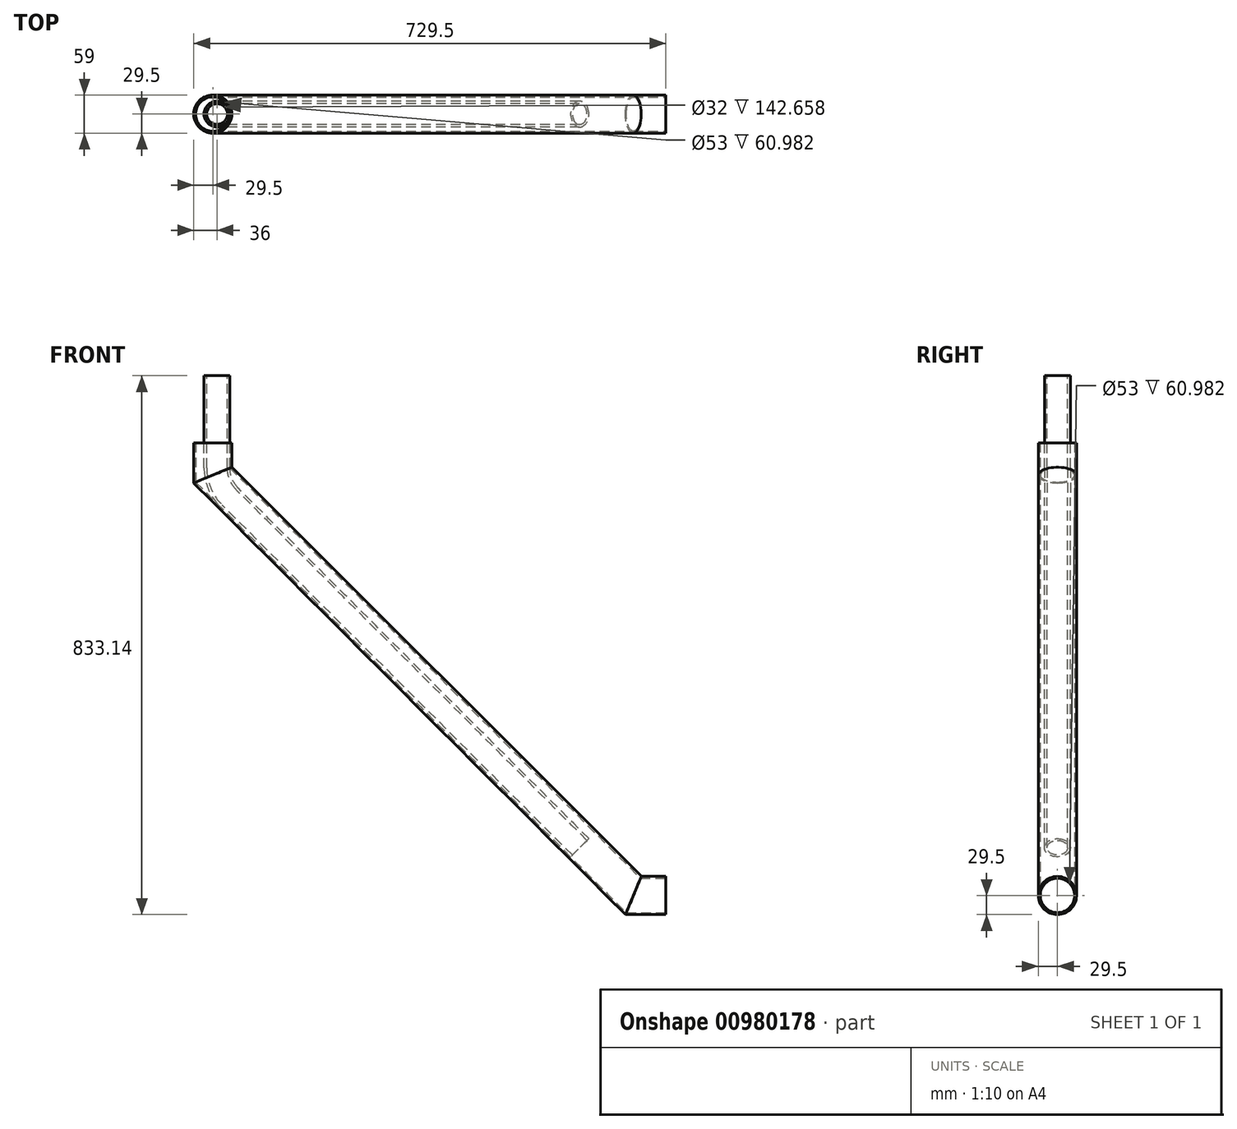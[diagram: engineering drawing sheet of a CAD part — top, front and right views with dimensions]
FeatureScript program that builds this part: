
annotation { "Feature Type Name" : "Feature", "Feature Type Description" : "" }
export const myFeature = defineFeature(function(context is Context, id is Id, definition is map)
    precondition{}
    {
        {
            var Q0;
            Q0=qCreatedBy(makeId("Top.planeOp"),FACE);
            var sketch = newSketch(context, id + "F0", { "sketchPlane" : qUnion([Q0])});
            skCircle(sketch, "E0", {"center": v(0, 0) * mm, "radius": 26.5 * mm});
            skCircle(sketch, "E1", {"center": v(0, 0) * mm, "radius": 29.5 * mm});
            skCircle(sketch, "E2", {"center": v(0, 0) * mm, "radius": 20 * mm, "construction": true});
            skSolve(sketch);
        }
        {
            var Q0;
            Q0=qCreatedBy(makeId("Front.planeOp"),FACE);
            var sketch = newSketch(context, id + "F1", { "sketchPlane" : qUnion([Q0])});
            skLineSegment(sketch, "E3", {"start": v(0, 0) * mm, "end": v(0, -50) * mm});
            skLineSegment(sketch, "E4", {"start": v(0, -50) * mm, "end": v(650, -700) * mm});
            skLineSegment(sketch, "E5", {"start": v(650, -700) * mm, "end": v(700, -700) * mm});
            skSolve(sketch);
        }
        {
            var Q0;
            Q0 = qSketchRegion(id + "F0", true);
            var Q1;
            Q1 = qConstructionFilter(qBodyType(qCreatedBy(id + "F1" ,EDGE), BodyType.WIRE), ConstructionObject.NO);
            sweep(context, id + "F2", {"profiles" : qUnion([Q0]), "path" : qUnion([Q1])});
        }
        {
            var Q0;
            Q0=qCreatedBy(makeId("Front.planeOp"),FACE);
            var sketch = newSketch(context, id + "F3", { "sketchPlane" : qUnion([Q0])});
            skLineSegment(sketch, "E6", {"start": v(50.18, -137.65) * mm, "end": v(-26.5, -60.98) * mm, "construction": true});
            skLineSegment(sketch, "E7", {"start": v(-26.5, -60.98) * mm, "end": v(-26.5, 0) * mm, "construction": true});
            skLineSegment(sketch, "E8", {"start": v(-26.5, 0) * mm, "end": v(0, 0) * mm, "construction": true});
            skLineSegment(sketch, "E9", {"start": v(0, 0) * mm, "end": v(26.5, 0) * mm, "construction": true});
            skLineSegment(sketch, "E10", {"start": v(26.5, 0) * mm, "end": v(26.5, -39.02) * mm, "construction": true});
            skLineSegment(sketch, "E11", {"start": v(26.5, -39.02) * mm, "end": v(93.16, -105.68) * mm, "construction": true});
            skLineSegment(sketch, "E12", {"start": v(0, 0) * mm, "end": v(0, -50) * mm, "construction": true});
            skLineSegment(sketch, "E13", {"start": v(0, -50) * mm, "end": v(72.4, -122.4) * mm, "construction": true});
            skLineSegment(sketch, "E14", {"start": v(6.5, 0) * mm, "end": v(6.5, -39.02) * mm});
            skArc(sketch, "E15", {"start": v(6.5, -39.02) * mm, "mid": v(11.4, -63.66) * mm, "end": v(25.36, -84.55) * mm});
            skLineSegment(sketch, "E16", {"start": v(25.36, -84.55) * mm, "end": v(566.96, -626.16) * mm});
            skLineSegment(sketch, "E17", {"start": v(6.5, -39.02) * mm, "end": v(26.5, -39.02) * mm, "construction": true});
            skLineSegment(sketch, "E18", {"start": v(6.5, 0) * mm, "end": v(6.5, 103.64) * mm});
            skSolve(sketch);
        }
        {
            var Q0;
            Q0=qCreatedBy(makeId("Top.planeOp"),FACE);
            var sketch = newSketch(context, id + "F4", { "sketchPlane" : qUnion([Q0])});
            skCircle(sketch, "E19", {"center": v(6.5, 0) * mm, "radius": 16 * mm});
            skCircle(sketch, "E20", {"center": v(6.5, 0) * mm, "radius": 20 * mm});
            skSolve(sketch);
        }
        {
            var Q0;
            Q0 = qSketchRegion(id + "F4", true);
            var Q1;
            Q1 = qConstructionFilter(qBodyType(qCreatedBy(id + "F3" ,EDGE), BodyType.WIRE), ConstructionObject.NO);
            sweep(context, id + "F5", {"operationType" : NewBodyOperationType.ADD, "profiles" : qUnion([Q0]), "path" : qUnion([Q1])});
        }
    });
